# Revit family: Sanitary_Taps-Mixers_hansgrohe_71465187-Hansgrohe-Basic-set-for-single_
name_source: partatom
category: Plumbing Fixtures
revit_build: Autodesk Revit 2015 (Build: 20140322_1515(x64)
units: mm (PartAtom-declared; Revit-internal decimal feet)

## types (1)
- n.a.
    BIMobject category = Taps & Mixers
    BIMobject category code = sanitary-taps-mixers
    BIMobject main category = Sanitary
    BIMobject main category code = sanitary
    Brand url = http://www.hansgrohe-int.com
    Default Elevation = 4' - 0"
    Design country = Germany
    Edition number = 1
    GTIN code = https://4059625293492
    IFC Classification = Sanitary Terminal
    Manufacturer country = Germany
    Manufacturer name = hansgrohe
    Material main = Chrome
    Product Guid = 31da756e-5f39-4117-bfa4-747db56d66d2
    Product SKU = 71465187
    Product certification = https://www.hansgrohe.com.cn
    Product data url = https://bimobject.com
    Product family = Concealed Basic set bath/shower mixers
    Product group = Hansgrohe
    Product name = 71465187 Hansgrohe Basic set for single lever bath mixer for concealed installation
    Product url = https://www.hansgrohe.com.cn
    QR code = http://bimobject.com
    Technical description = https://www.hansgrohe.com.cn

## geometry (parser evidence)
native form markers: Sweep x2
no freeform markers — native parametric forms only
